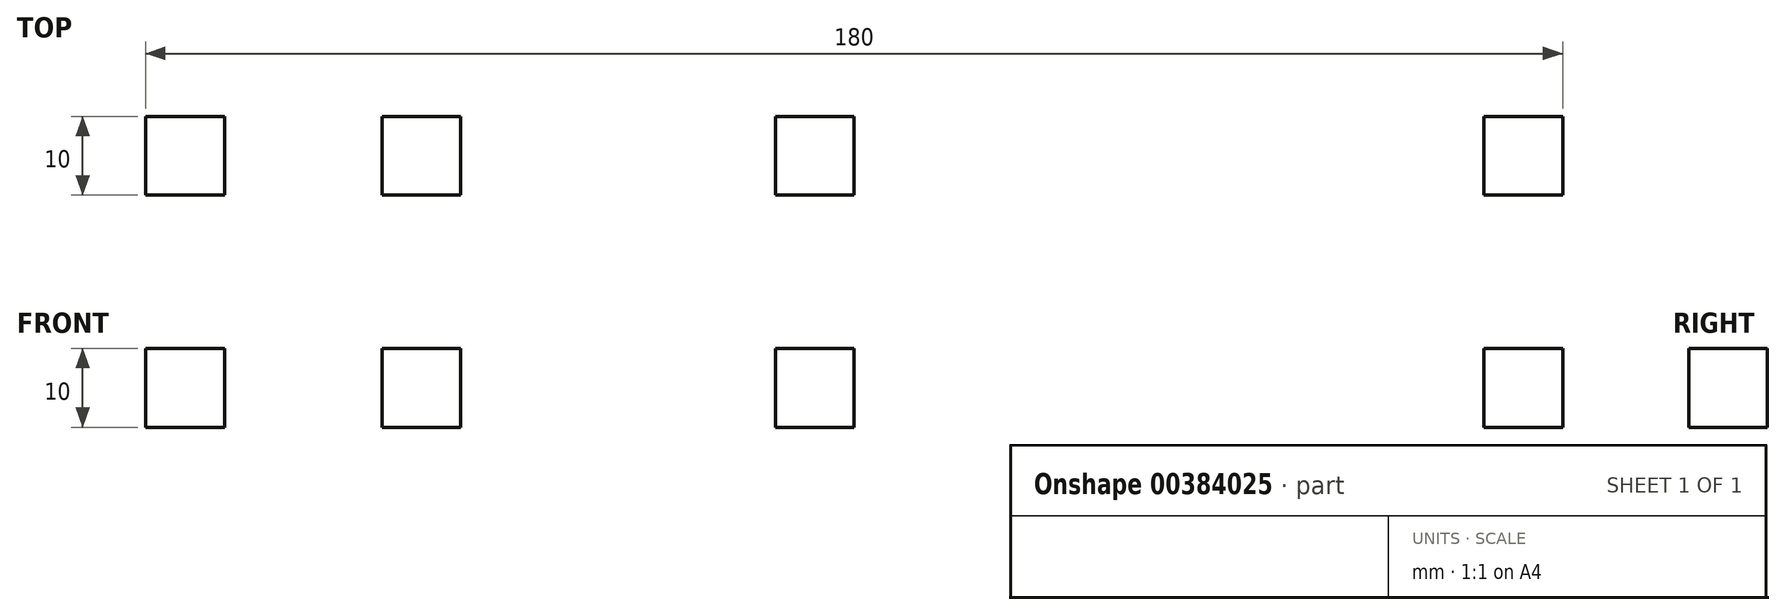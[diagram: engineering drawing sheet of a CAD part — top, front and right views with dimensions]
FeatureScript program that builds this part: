
annotation { "Feature Type Name" : "Feature", "Feature Type Description" : "" }
export const myFeature = defineFeature(function(context is Context, id is Id, definition is map)
    precondition{}
    {
        {
            var Q0;
            Q0=qCreatedBy(makeId("Top.planeOp"),FACE);
            var sketch = newSketch(context, id + "F0", { "sketchPlane" : qUnion([Q0])});
            skLineSegment(sketch, "E0.bottom", {"start": v(-10, 10) * mm, "end": v(0, 10) * mm});
            skLineSegment(sketch, "E0.top", {"start": v(-10, 0) * mm, "end": v(0, 0) * mm});
            skLineSegment(sketch, "E0.left", {"start": v(-10, 10) * mm, "end": v(-10, 0) * mm});
            skLineSegment(sketch, "E0.right", {"start": v(0, 10) * mm, "end": v(0, 0) * mm});
            skLineSegment(sketch, "E1", {"start": v(0, 0) * mm, "end": v(20, 0) * mm, "construction": true});
            skLineSegment(sketch, "E2", {"start": v(10, 0) * mm, "end": v(10, -7.49) * mm, "construction": true});
            skPoint(sketch, "E2.endSnap0", {"position": v(10, 0) * mm});
            skLineSegment(sketch, "E3.MirrorCS", {"start": v(30, 10) * mm, "end": v(20, 10) * mm});
            skLineSegment(sketch, "E4.MirrorCS", {"start": v(20, 10) * mm, "end": v(20, 0) * mm});
            skLineSegment(sketch, "E5.MirrorCS", {"start": v(30, 0) * mm, "end": v(20, 0) * mm});
            skLineSegment(sketch, "E6.MirrorCS", {"start": v(30, 10) * mm, "end": v(30, 0) * mm});
            skLineSegment(sketch, "E7", {"start": v(30, 0) * mm, "end": v(70, 0) * mm, "construction": true});
            skLineSegment(sketch, "E8.bottom", {"start": v(70, 0) * mm, "end": v(80, 0) * mm});
            skLineSegment(sketch, "E8.top", {"start": v(70, 10) * mm, "end": v(80, 10) * mm});
            skLineSegment(sketch, "E8.left", {"start": v(70, 0) * mm, "end": v(70, 10) * mm});
            skLineSegment(sketch, "E8.right", {"start": v(80, 0) * mm, "end": v(80, 10) * mm});
            skLineSegment(sketch, "E9", {"start": v(80, 0) * mm, "end": v(160, 0) * mm, "construction": true});
            skLineSegment(sketch, "E10.bottom", {"start": v(160, 0) * mm, "end": v(170, 0) * mm});
            skLineSegment(sketch, "E10.top", {"start": v(160, 10) * mm, "end": v(170, 10) * mm});
            skLineSegment(sketch, "E10.left", {"start": v(160, 0) * mm, "end": v(160, 10) * mm});
            skLineSegment(sketch, "E10.right", {"start": v(170, 0) * mm, "end": v(170, 10) * mm});
            skSolve(sketch);
        }
        {
            var Q0;
            Q0=makeQuery(id+"F0.imprint","IMPRINT",FACE,{"disambiguationData":[TD([[makeQuery(id+"F0.imprint","IMPRINT",EDGE,{"derivedFrom":sQuery(id+"F0.wireOp",EDGE,"E0.bottom")}),-1.0]])]});
            var Q1;
            Q1=makeQuery(id+"F0.imprint","IMPRINT",FACE,{"disambiguationData":[TD([[makeQuery(id+"F0.imprint","IMPRINT",EDGE,{"derivedFrom":sQuery(id+"F0.wireOp",EDGE,"E3.MirrorCS")}),1.0]])]});
            var Q2;
            Q2=makeQuery(id+"F0.imprint","IMPRINT",FACE,{"disambiguationData":[TD([[makeQuery(id+"F0.imprint","IMPRINT",EDGE,{"derivedFrom":sQuery(id+"F0.wireOp",EDGE,"E8.bottom")}),1.0]])]});
            var Q3;
            Q3=makeQuery(id+"F0.imprint","IMPRINT",FACE,{"disambiguationData":[TD([[makeQuery(id+"F0.imprint","IMPRINT",EDGE,{"derivedFrom":sQuery(id+"F0.wireOp",EDGE,"E10.bottom")}),1.0]])]});
            extrude(context, id + "F1", {"entities" : qUnion([Q0, Q1, Q2, Q3]), "depth" : 10 * mm});
        }
    });
